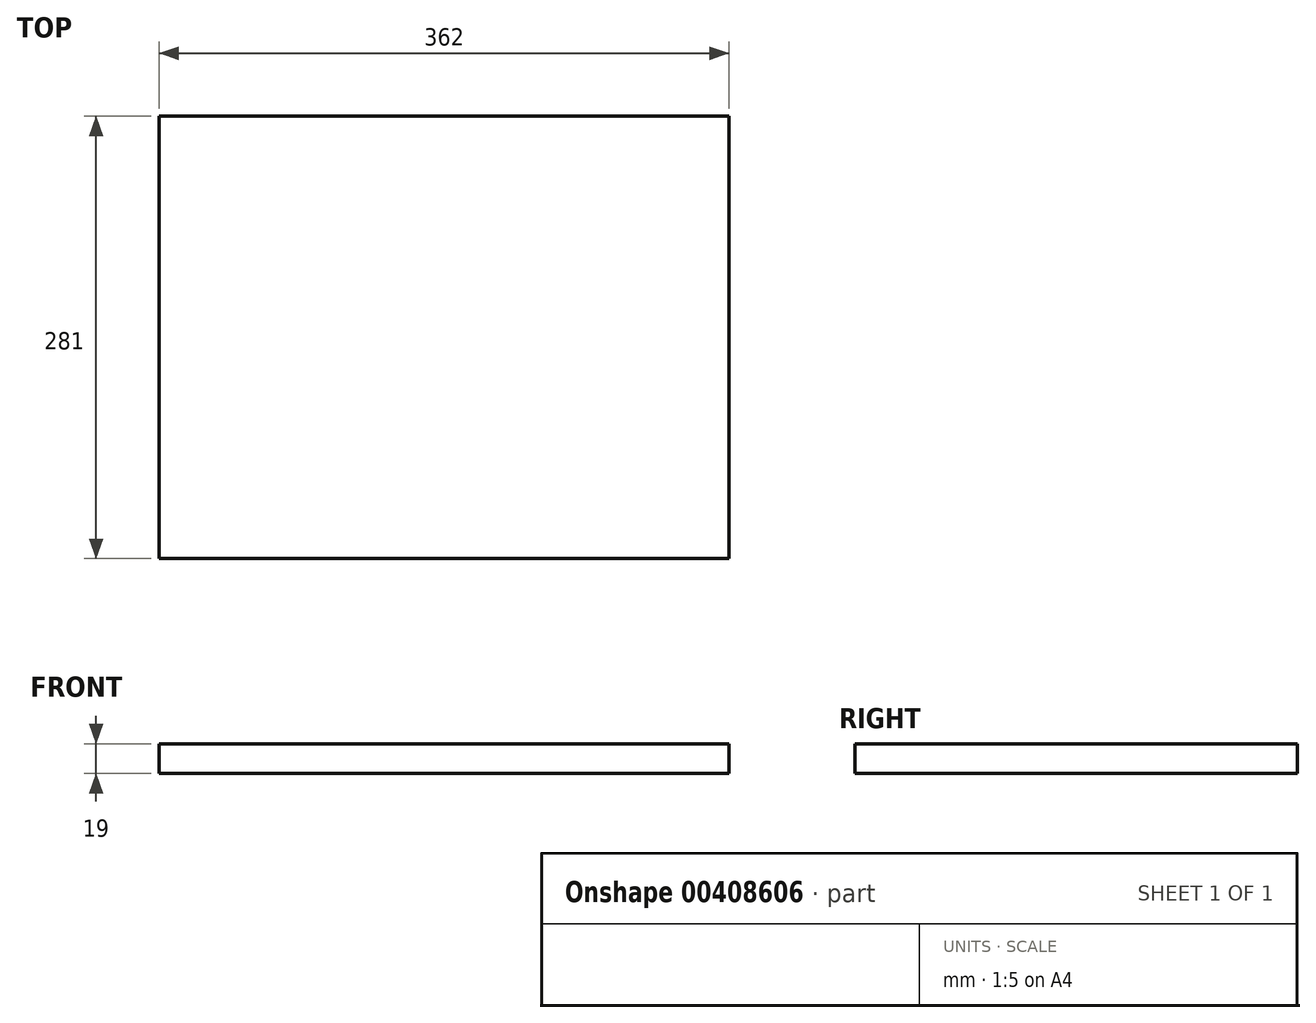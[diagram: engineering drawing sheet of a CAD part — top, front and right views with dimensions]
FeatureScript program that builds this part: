
annotation { "Feature Type Name" : "Feature", "Feature Type Description" : "" }
export const myFeature = defineFeature(function(context is Context, id is Id, definition is map)
    precondition{}
    {
        {
            var Q0;
            Q0=qCreatedBy(makeId("Front.planeOp"),FACE);
            var sketch = newSketch(context, id + "F0", { "sketchPlane" : qUnion([Q0])});
            skLineSegment(sketch, "E0.bottom", {"start": v(0, 0) * mm, "end": v(362, 0) * mm});
            skLineSegment(sketch, "E0.top", {"start": v(0, 19) * mm, "end": v(362, 19) * mm});
            skLineSegment(sketch, "E0.left", {"start": v(0, 0) * mm, "end": v(0, 19) * mm});
            skLineSegment(sketch, "E0.right", {"start": v(362, 0) * mm, "end": v(362, 19) * mm});
            skSolve(sketch);
        }
        {
            var Q0;
            Q0 = qSketchRegion(id + "F0", true);
            extrude(context, id + "F1", {"entities" : qUnion([Q0]), "depth" : 281 * mm});
        }
    });
